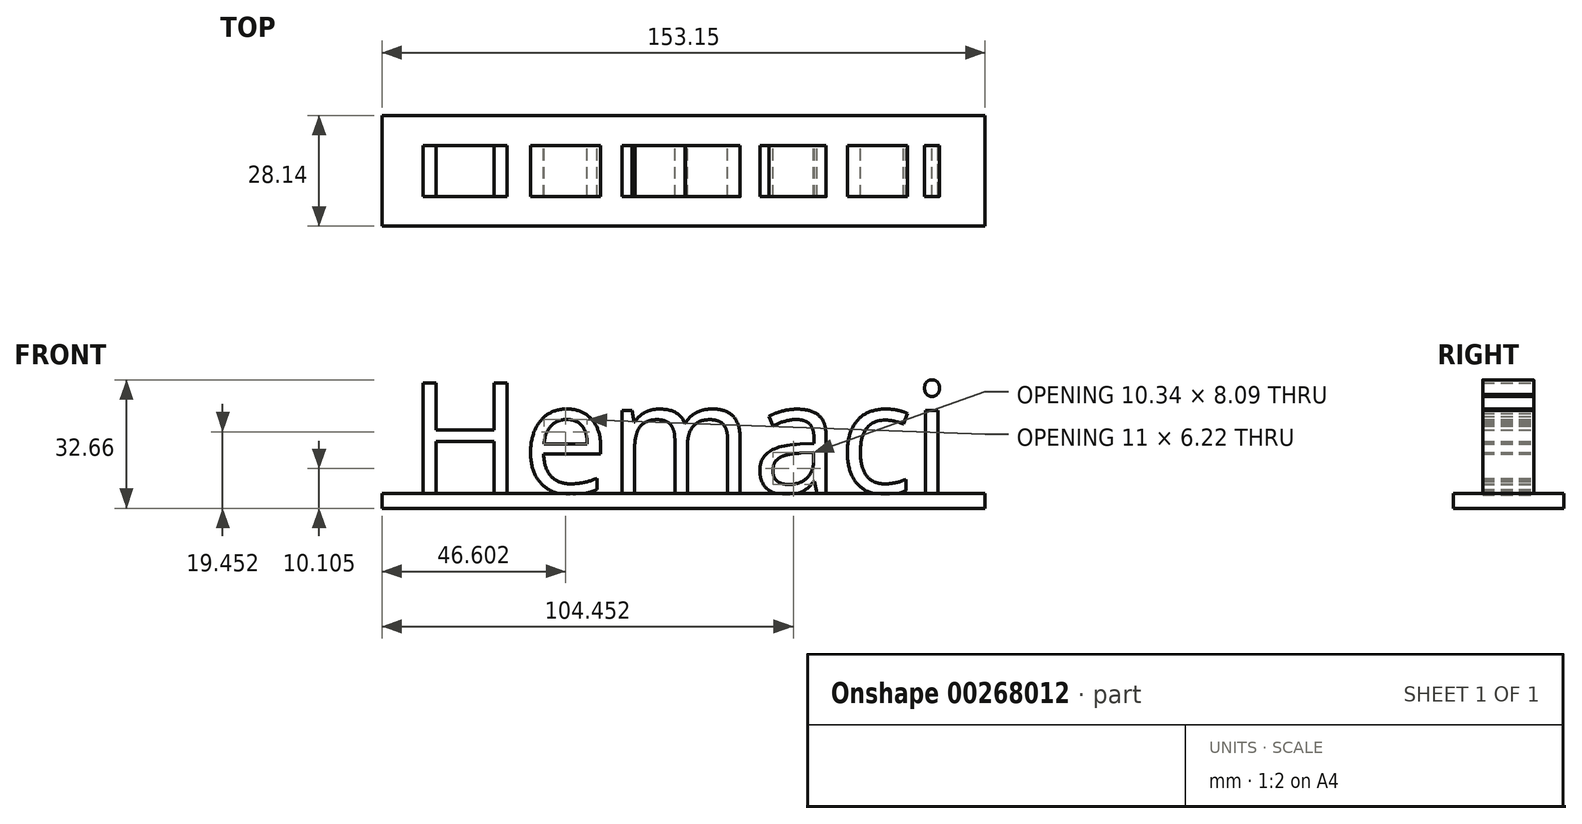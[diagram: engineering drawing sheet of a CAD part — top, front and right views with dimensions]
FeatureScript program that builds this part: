
annotation { "Feature Type Name" : "Feature", "Feature Type Description" : "" }
export const myFeature = defineFeature(function(context is Context, id is Id, definition is map)
    precondition{}
    {
        {
            var Q0;
            Q0=qCreatedBy(makeId("Front.planeOp"),FACE);
            var sketch = newSketch(context, id + "F0", { "sketchPlane" : qUnion([Q0])});
            skText(sketch, "E0", { "text": "Hemaci\n", "fontName": "OpenSans-Regular.ttf"});
            const initialGuessF0  = {"E0": [-0.0769, 0, 1, 0, 0.0283]};
            skSetInitialGuess(sketch, initialGuessF0);
            skSolve(sketch);
        }
        {
            var Q0;
            Q0 = qSketchRegion(id + "F0", true);
            extrude(context, id + "F1", {"entities" : qUnion([Q0]), "depth" : 12.95 * mm});
        }
        {
            var Q0;
            Q0=qCreatedBy(makeId("Top.planeOp"),FACE);
            var sketch = newSketch(context, id + "F2", { "sketchPlane" : qUnion([Q0])});
            skLineSegment(sketch, "E1.bottom", {"start": v(-83.42, -20.45) * mm, "end": v(69.73, -20.45) * mm});
            skLineSegment(sketch, "E1.top", {"start": v(-83.42, 7.7) * mm, "end": v(69.73, 7.7) * mm});
            skLineSegment(sketch, "E1.left", {"start": v(-83.42, -20.45) * mm, "end": v(-83.42, 7.7) * mm});
            skLineSegment(sketch, "E1.right", {"start": v(69.73, -20.45) * mm, "end": v(69.73, 7.7) * mm});
            skSolve(sketch);
        }
        {
            var Q0;
            Q0 = qSketchRegion(id + "F2", true);
            extrude(context, id + "F3", {"entities" : qUnion([Q0]), "oppositeDirection" : true, "depth" : 3.8 * mm});
        }
    });
